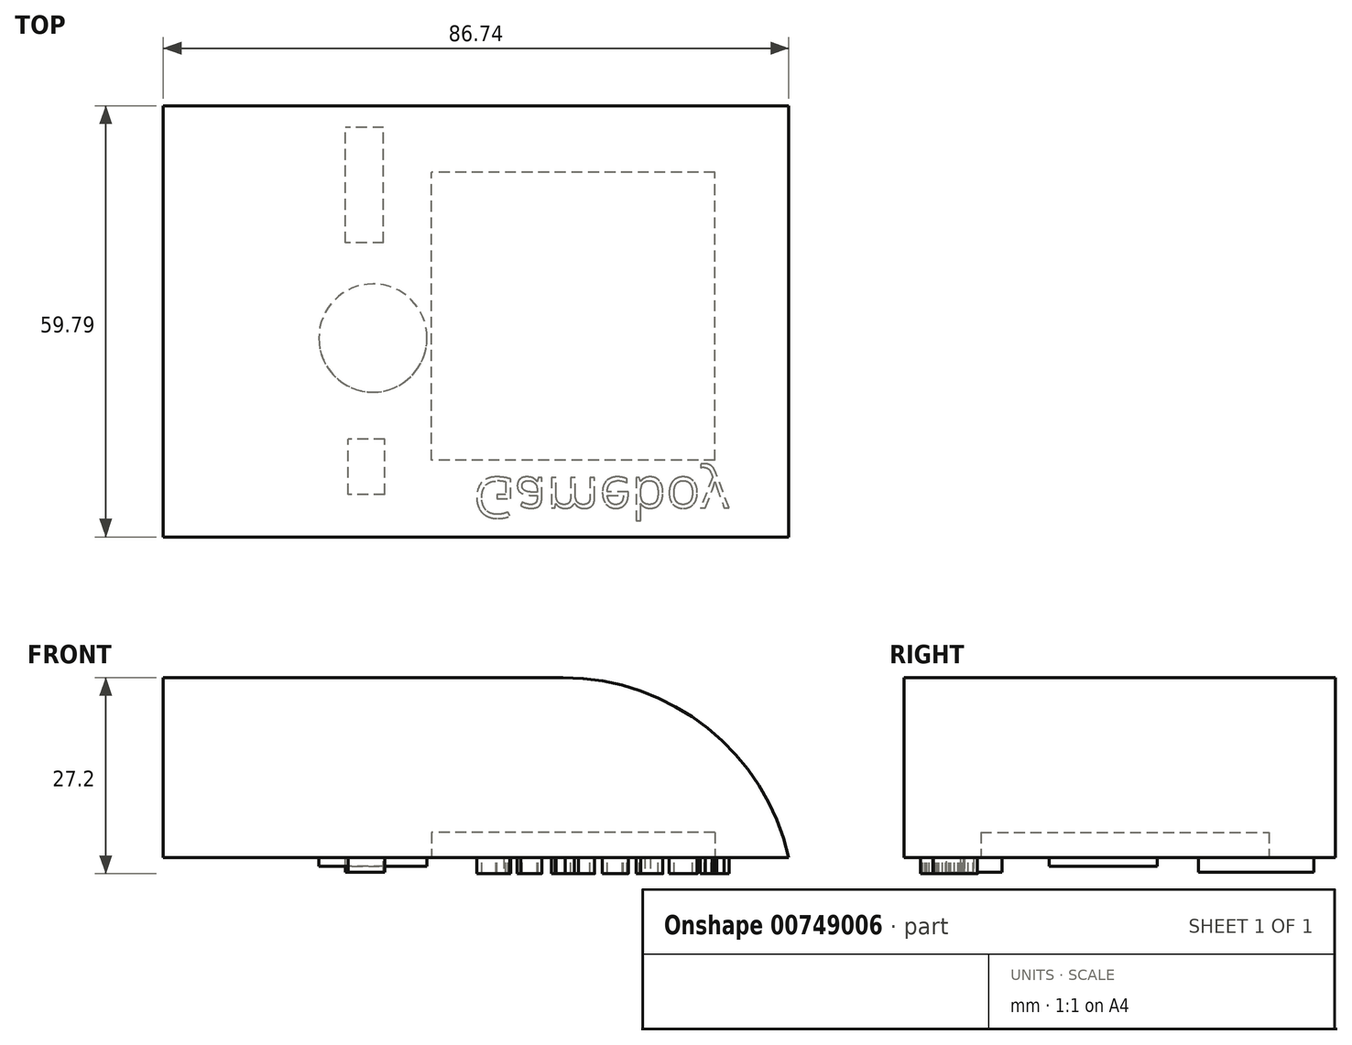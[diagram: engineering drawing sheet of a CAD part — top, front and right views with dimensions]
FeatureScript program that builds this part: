
annotation { "Feature Type Name" : "Feature", "Feature Type Description" : "" }
export const myFeature = defineFeature(function(context is Context, id is Id, definition is map)
    precondition{}
    {
        {
            var Q0;
            Q0=qCreatedBy(makeId("Top.planeOp"),FACE);
            var sketch = newSketch(context, id + "F0", { "sketchPlane" : qUnion([Q0])});
            skLineSegment(sketch, "E0.bottom", {"start": v(-106.93, 32.2) * mm, "end": v(-20.19, 32.2) * mm});
            skLineSegment(sketch, "E0.top", {"start": v(-106.93, -27.6) * mm, "end": v(-20.19, -27.6) * mm});
            skLineSegment(sketch, "E0.left", {"start": v(-106.93, 32.2) * mm, "end": v(-106.93, -27.6) * mm});
            skLineSegment(sketch, "E0.right", {"start": v(-20.19, 32.2) * mm, "end": v(-20.19, -27.6) * mm});
            skSolve(sketch);
        }
        {
            var Q0;
            Q0 = qSketchRegion(id + "F0", true);
            extrude(context, id + "F1", {"entities" : qUnion([Q0]), "depth" : 25 * mm, "offsetDistance" : 25 * mm});
        }
        {
            var Q0;
            Q0=makeQuery(id+"F1.opExtrude","CAP_EDGE",EDGE,{"disambiguationData":[OSD([sQuery(id+"F0.wireOp",EDGE,"E0.right")])],"isStart":false});
            fillet(context, id + "F2", {"entities" : qUnion([Q0]), "radius" : 32.1 * mm, "tangentPropagation" : true, "allowEdgeOverflow" : false});
        }
        {
            var Q0;
            Q0=makeQuery(id+"F1.opExtrude","CAP_FACE",FACE,{"disambiguationData":[OSD([sQuery(id+"F0.wireOp",EDGE,"E0.bottom"),sQuery(id+"F0.wireOp",EDGE,"E0.top"),sQuery(id+"F0.wireOp",EDGE,"E0.left"),sQuery(id+"F0.wireOp",EDGE,"E0.right")])],"isStart":true});
            var sketch = newSketch(context, id + "F3", { "sketchPlane" : qUnion([Q0])});
            skLineSegment(sketch, "E1.bottom", {"start": v(-30.44, 16.96) * mm, "end": v(-69.73, 16.96) * mm});
            skLineSegment(sketch, "E1.top", {"start": v(-30.44, -22.97) * mm, "end": v(-69.73, -22.97) * mm});
            skLineSegment(sketch, "E1.left", {"start": v(-30.44, 16.96) * mm, "end": v(-30.44, -22.97) * mm});
            skLineSegment(sketch, "E1.right", {"start": v(-69.73, 16.96) * mm, "end": v(-69.73, -22.97) * mm});
            skSolve(sketch);
        }
        {
            var Q0;
            Q0=makeQuery(id+"F3.imprint","IMPRINT",FACE,{"disambiguationData":[TD([[makeQuery(id+"F3.imprint","IMPRINT",EDGE,{"derivedFrom":sQuery(id+"F3.wireOp",EDGE,"E1.bottom")}),1.0]])]});
            extrude(context, id + "F4", {"entities" : qUnion([Q0]), "operationType" : NewBodyOperationType.ADD, "depth" : 25 * mm, "offsetDistance" : 25 * mm});
        }
        {
            var Q0;
            Q0=makeQuery(id+"F4.opExtrude","CAP_FACE",FACE,{"disambiguationData":[OSD([sQuery(id+"F3.wireOp",EDGE,"E1.bottom"),sQuery(id+"F3.wireOp",EDGE,"E1.top"),sQuery(id+"F3.wireOp",EDGE,"E1.left"),sQuery(id+"F3.wireOp",EDGE,"E1.right")])],"isStart":false});
            extrude(context, id + "F5", {"entities" : qUnion([Q0]), "operationType" : NewBodyOperationType.REMOVE, "oppositeDirection" : true, "depth" : 28.5 * mm, "offsetDistance" : 25 * mm});
        }
        {
            var Q0;
            Q0=makeQuery(id+"F1.opExtrude","CAP_FACE",FACE,{"disambiguationData":[OSD([sQuery(id+"F0.wireOp",EDGE,"E0.bottom"),sQuery(id+"F0.wireOp",EDGE,"E0.top"),sQuery(id+"F0.wireOp",EDGE,"E0.left"),sQuery(id+"F0.wireOp",EDGE,"E0.right")])],"isStart":true});
            var sketch = newSketch(context, id + "F6", { "sketchPlane" : qUnion([Q0])});
            skLineSegment(sketch, "E2.bottom", {"start": v(-76.22, 21.68) * mm, "end": v(-81.34, 21.68) * mm});
            skLineSegment(sketch, "E2.top", {"start": v(-76.22, 14.02) * mm, "end": v(-81.34, 14.02) * mm});
            skLineSegment(sketch, "E2.left", {"start": v(-76.22, 21.68) * mm, "end": v(-76.22, 14.02) * mm});
            skLineSegment(sketch, "E2.right", {"start": v(-81.34, 21.68) * mm, "end": v(-81.34, 14.02) * mm});
            skLineSegment(sketch, "E3.bottom", {"start": v(-76.53, 8.54) * mm, "end": v(-81.34, 8.54) * mm});
            skLineSegment(sketch, "E3.top", {"start": v(-76.53, 0) * mm, "end": v(-81.34, 0) * mm});
            skLineSegment(sketch, "E3.left", {"start": v(-76.53, 8.54) * mm, "end": v(-76.53, 0) * mm});
            skLineSegment(sketch, "E3.right", {"start": v(-81.34, 8.54) * mm, "end": v(-81.34, 0) * mm});
            skLineSegment(sketch, "E4.bottom", {"start": v(-76.67, -4.8) * mm, "end": v(-81.34, -4.8) * mm});
            skLineSegment(sketch, "E4.top", {"start": v(-76.67, -13.28) * mm, "end": v(-81.34, -13.28) * mm});
            skLineSegment(sketch, "E4.left", {"start": v(-76.67, -4.8) * mm, "end": v(-76.67, -13.28) * mm});
            skLineSegment(sketch, "E4.right", {"start": v(-81.34, -4.8) * mm, "end": v(-81.34, -13.28) * mm});
            skSolve(sketch);
        }
        {
            var Q0;
            Q0=makeQuery(id+"F6.imprint","IMPRINT",FACE,{"disambiguationData":[TD([[makeQuery(id+"F6.imprint","IMPRINT",EDGE,{"derivedFrom":sQuery(id+"F6.wireOp",EDGE,"E2.bottom")}),1.0]])]});
            extrude(context, id + "F7", {"entities" : qUnion([Q0]), "operationType" : NewBodyOperationType.ADD, "depth" : 2 * mm, "offsetDistance" : 25 * mm});
        }
        {
            var Q0;
            Q0=makeQuery(id+"F1.opExtrude","CAP_FACE",FACE,{"disambiguationData":[OSD([sQuery(id+"F0.wireOp",EDGE,"E0.bottom"),sQuery(id+"F0.wireOp",EDGE,"E0.top"),sQuery(id+"F0.wireOp",EDGE,"E0.left"),sQuery(id+"F0.wireOp",EDGE,"E0.right")])],"isStart":true});
            var sketch = newSketch(context, id + "F8", { "sketchPlane" : qUnion([Q0])});
            skCircle(sketch, "E5", {"center": v(-77.86, 0) * mm, "radius": 7.5 * mm});
            skSolve(sketch);
        }
        {
            var Q0;
            Q0=makeQuery(id+"F8.imprint","IMPRINT",FACE,{"disambiguationData":[TD([[makeQuery(id+"F8.imprint","IMPRINT",EDGE,{"derivedFrom":sQuery(id+"F8.wireOp",EDGE,"E5")}),1.0]])]});
            extrude(context, id + "F9", {"entities" : qUnion([Q0]), "operationType" : NewBodyOperationType.ADD, "depth" : 1.2 * mm, "offsetDistance" : 25 * mm});
        }
        {
            var Q0;
            Q0=makeQuery(id+"F1.opExtrude","CAP_FACE",FACE,{"disambiguationData":[OSD([sQuery(id+"F0.wireOp",EDGE,"E0.bottom"),sQuery(id+"F0.wireOp",EDGE,"E0.top"),sQuery(id+"F0.wireOp",EDGE,"E0.left"),sQuery(id+"F0.wireOp",EDGE,"E0.right")])],"isStart":true});
            var sketch = newSketch(context, id + "F10", { "sketchPlane" : qUnion([Q0])});
            skLineSegment(sketch, "E6.bottom", {"start": v(-76.4, -13.22) * mm, "end": v(-81.71, -13.22) * mm});
            skLineSegment(sketch, "E6.top", {"start": v(-76.4, -29.22) * mm, "end": v(-81.71, -29.22) * mm});
            skLineSegment(sketch, "E6.left", {"start": v(-76.4, -13.22) * mm, "end": v(-76.4, -29.22) * mm});
            skLineSegment(sketch, "E6.right", {"start": v(-81.71, -13.22) * mm, "end": v(-81.71, -29.22) * mm});
            skSolve(sketch);
        }
        {
            var Q0;
            Q0=makeQuery(id+"F10.imprint","IMPRINT",FACE,{"disambiguationData":[TD([[makeQuery(id+"F10.imprint","IMPRINT",EDGE,{"derivedFrom":sQuery(id+"F10.wireOp",EDGE,"E6.bottom")}),1.0]])]});
            extrude(context, id + "F11", {"entities" : qUnion([Q0]), "operationType" : NewBodyOperationType.ADD, "depth" : 2 * mm, "offsetDistance" : 25 * mm});
        }
        {
            var Q0;
            Q0=makeQuery(id+"F1.opExtrude","CAP_FACE",FACE,{"disambiguationData":[OSD([sQuery(id+"F0.wireOp",EDGE,"E0.bottom"),sQuery(id+"F0.wireOp",EDGE,"E0.top"),sQuery(id+"F0.wireOp",EDGE,"E0.left"),sQuery(id+"F0.wireOp",EDGE,"E0.right")])],"isStart":true});
            var sketch = newSketch(context, id + "F12", { "sketchPlane" : qUnion([Q0])});
            skText(sketch, "E7", { "text": "Gameboy\n", "fontName": "OpenSans-Regular.ttf"});
            const initialGuessF12  = {"E7": [-0.06395, 0.01933, 1, 0, 0.00568]};
            skSetInitialGuess(sketch, initialGuessF12);
            skSolve(sketch);
        }
        {
            var Q0;
            Q0 = qSketchRegion(id + "F12", true);
            extrude(context, id + "F13", {"entities" : qUnion([Q0]), "operationType" : NewBodyOperationType.ADD, "depth" : 2.2 * mm, "offsetDistance" : 25 * mm});
        }
    });
